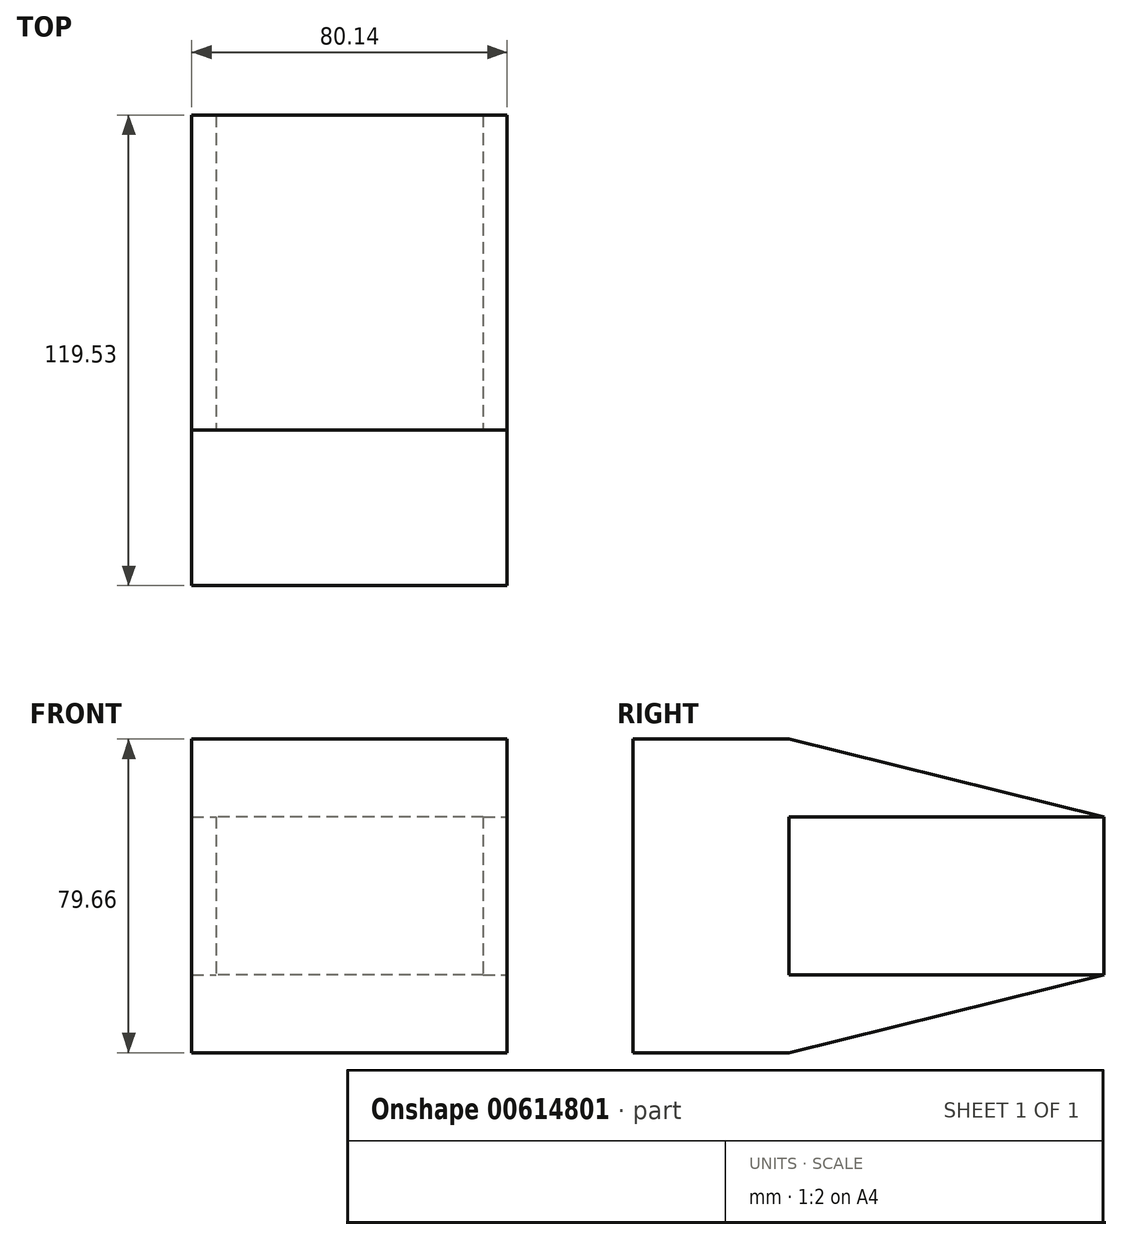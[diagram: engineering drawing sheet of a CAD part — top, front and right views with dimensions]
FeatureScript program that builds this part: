
annotation { "Feature Type Name" : "Feature", "Feature Type Description" : "" }
export const myFeature = defineFeature(function(context is Context, id is Id, definition is map)
    precondition{}
    {
        {
            var Q0;
            Q0=qCreatedBy(makeId("Front.planeOp"),FACE);
            var sketch = newSketch(context, id + "F0", { "sketchPlane" : qUnion([Q0])});
            skLineSegment(sketch, "E0.bottom", {"start": v(-40.07, 39.83) * mm, "end": v(40.07, 39.83) * mm});
            skLineSegment(sketch, "E0.top", {"start": v(-40.07, -39.83) * mm, "end": v(40.07, -39.83) * mm});
            skLineSegment(sketch, "E0.left", {"start": v(-40.07, 39.83) * mm, "end": v(-40.07, -39.83) * mm});
            skLineSegment(sketch, "E0.right", {"start": v(40.07, 39.83) * mm, "end": v(40.07, -39.83) * mm});
            skSolve(sketch);
        }
        {
            var Q0;
            Q0 = qSketchRegion(id + "F0", true);
            extrude(context, id + "F1", {"entities" : qUnion([Q0]), "depth" : 39.53 * mm, "offsetDistance" : 25 * mm});
        }
        {
            var Q0;
            Q0=makeQuery(id+"F1.opExtrude","CAP_FACE",FACE,{"disambiguationData":[OSD([sQuery(id+"F0.wireOp",EDGE,"E0.bottom"),sQuery(id+"F0.wireOp",EDGE,"E0.top"),sQuery(id+"F0.wireOp",EDGE,"E0.left"),sQuery(id+"F0.wireOp",EDGE,"E0.right")])],"isStart":true});
            var sketch = newSketch(context, id + "F2", { "sketchPlane" : qUnion([Q0])});
            skLineSegment(sketch, "E1.bottom", {"start": v(-33.95, 20.12) * mm, "end": v(33.95, 20.12) * mm});
            skLineSegment(sketch, "E1.top", {"start": v(-33.95, -20.12) * mm, "end": v(33.95, -20.12) * mm});
            skLineSegment(sketch, "E1.left", {"start": v(-33.95, 20.12) * mm, "end": v(-33.95, -20.12) * mm});
            skLineSegment(sketch, "E1.right", {"start": v(33.95, 20.12) * mm, "end": v(33.95, -20.12) * mm});
            skSolve(sketch);
        }
        {
            var Q0;
            Q0 = qSketchRegion(id + "F2", true);
            extrude(context, id + "F3", {"entities" : qUnion([Q0]), "operationType" : NewBodyOperationType.ADD, "depth" : 80 * mm, "offsetDistance" : 25 * mm});
        }
        {
            var Q0;
            Q0=makeQuery(id+"F1.opExtrude","SWEPT_FACE",FACE,{"disambiguationData":[OSD([sQuery(id+"F0.wireOp",EDGE,"E0.right")])]});
            var sketch = newSketch(context, id + "F4", { "sketchPlane" : qUnion([Q0])});
            skLineSegment(sketch, "E2.0", {"start": v(0, 39.83) * mm, "end": v(0, -39.83) * mm});
            skLineSegment(sketch, "E3.0", {"start": v(80, 20.12) * mm, "end": v(0, 20.12) * mm});
            skLineSegment(sketch, "E4.0", {"start": v(-39.53, 39.83) * mm, "end": v(0, 39.83) * mm});
            skLineSegment(sketch, "E5", {"start": v(0, 39.83) * mm, "end": v(0, 20.12) * mm});
            skLineSegment(sketch, "E6", {"start": v(80, 20.12) * mm, "end": v(0, 39.83) * mm});
            skLineSegment(sketch, "E7.0", {"start": v(80, -20.12) * mm, "end": v(0, -20.12) * mm});
            skLineSegment(sketch, "E8", {"start": v(0, -39.83) * mm, "end": v(0, -20.12) * mm});
            skLineSegment(sketch, "E9", {"start": v(80, -20.12) * mm, "end": v(0, -39.83) * mm});
            skSolve(sketch);
        }
        {
            var Q0;
            Q0 = qSketchRegion(id + "F4", true);
            var Q1;
            Q1=makeQuery(id+"F4.imprint","IMPRINT",FACE,{"disambiguationData":[TD([[makeQuery(id+"F4.imprint","IMPRINT",EDGE,{"derivedFrom":sQuery(id+"F4.wireOp",EDGE,"E2.0")}),-1.0]])]});
            var Q2;
            Q2=makeQuery(id+"F1.opExtrude","SWEPT_FACE",FACE,{"disambiguationData":[OSD([sQuery(id+"F0.wireOp",EDGE,"E0.left")])]});
            extrude(context, id + "F5", {"entities" : qUnion([Q0, Q1]), "operationType" : NewBodyOperationType.ADD, "endBound" : BoundingType.UP_TO_SURFACE, "oppositeDirection" : true, "depth" : 25 * mm, "endBoundEntityFace" : qUnion([Q2]), "offsetDistance" : 25 * mm});
        }
    });
